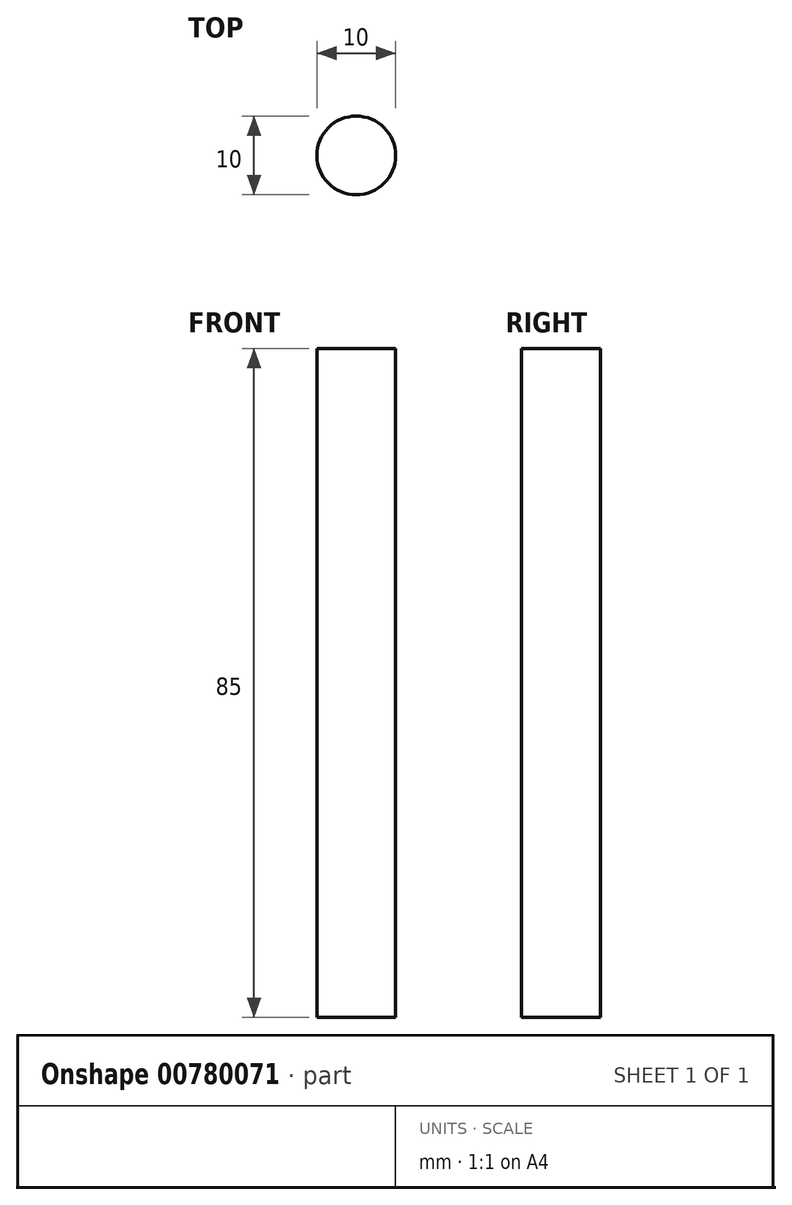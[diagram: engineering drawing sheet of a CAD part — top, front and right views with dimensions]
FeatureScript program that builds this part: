
annotation { "Feature Type Name" : "Feature", "Feature Type Description" : "" }
export const myFeature = defineFeature(function(context is Context, id is Id, definition is map)
    precondition{}
    {
        {
            var Q0;
            Q0=qCreatedBy(makeId("Top.planeOp"),FACE);
            var sketch = newSketch(context, id + "F0", { "sketchPlane" : qUnion([Q0])});
            skCircle(sketch, "E0", {"center": v(0, 0) * mm, "radius": 5 * mm});
            skSolve(sketch);
        }
        {
            var Q0;
            Q0 = qSketchRegion(id + "F0", true);
            extrude(context, id + "F1", {"entities" : qUnion([Q0]), "depth" : 85 * mm, "offsetDistance" : 25 * mm});
        }
    });
